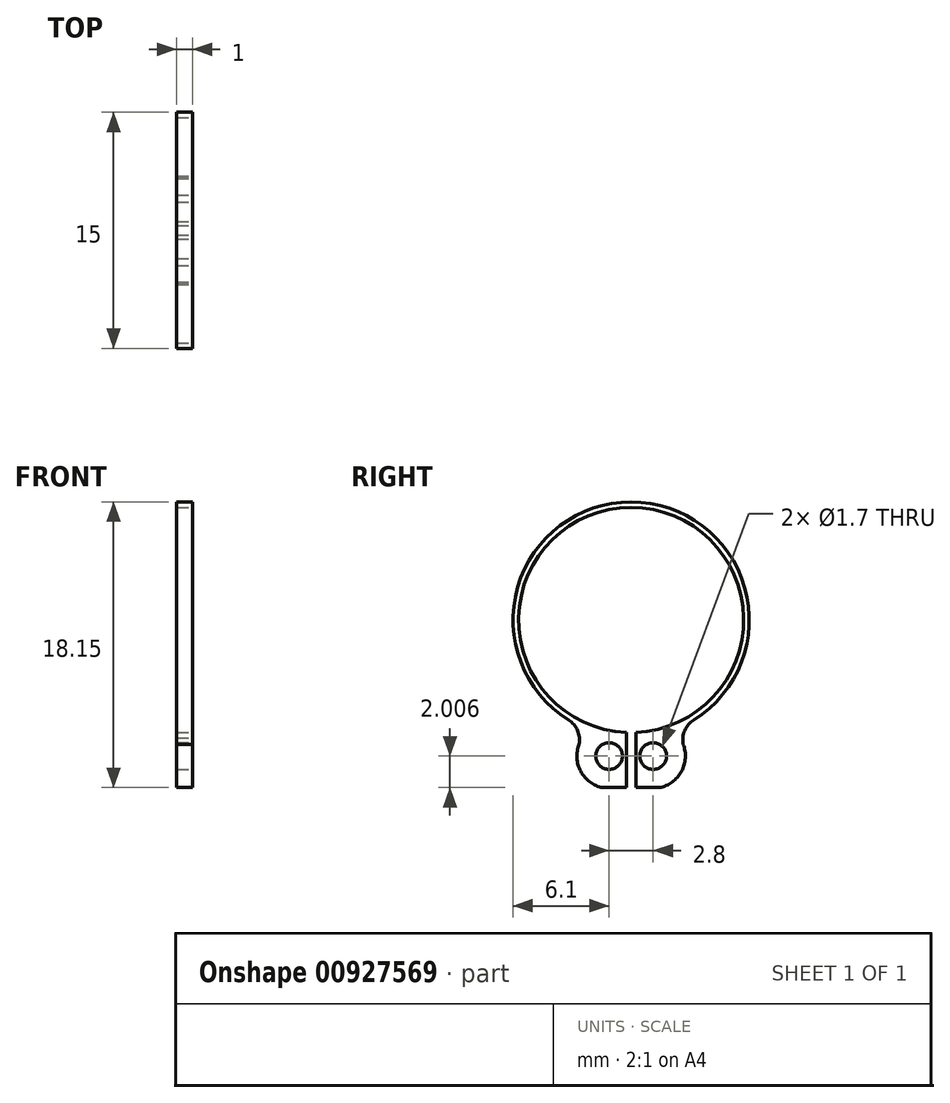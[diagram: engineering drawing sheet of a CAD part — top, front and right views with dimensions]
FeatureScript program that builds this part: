
annotation { "Feature Type Name" : "Feature", "Feature Type Description" : "" }
export const myFeature = defineFeature(function(context is Context, id is Id, definition is map)
    precondition{}
    {
        {
            var Q0;
            Q0=qCreatedBy(makeId("Right.planeOp"),FACE);
            var sketch = newSketch(context, id + "F0", { "sketchPlane" : qUnion([Q0])});
            skArc(sketch, "E0", {"start": v(0.3, -7.14) * mm, "mid": v(0, 7.15) * mm, "end": v(-0.3, -7.14) * mm});
            skArc(sketch, "E1", {"start": v(3.98, -6.36) * mm, "mid": v(0, 7.5) * mm, "end": v(-3.98, -6.36) * mm});
            skLineSegment(sketch, "E2", {"start": v(-7.47, -10.65) * mm, "end": v(-0.3, -10.65) * mm, "construction": true});
            skLineSegment(sketch, "E3", {"start": v(0.3, -7.14) * mm, "end": v(0.3, -10.65) * mm});
            skLineSegment(sketch, "E4.MirrorCS", {"start": v(-0.3, -7.14) * mm, "end": v(-0.3, -10.65) * mm});
            skCircle(sketch, "E5", {"center": v(1.4, -8.64) * mm, "radius": 0.85 * mm});
            skLineSegment(sketch, "E6", {"start": v(0.3, -10.65) * mm, "end": v(1.8, -10.65) * mm});
            skArc(sketch, "E7", {"start": v(1.8, -10.65) * mm, "mid": v(3.2, -9.62) * mm, "end": v(3.3, -7.9) * mm});
            skArc(sketch, "E8", {"start": v(3.3, -7.9) * mm, "mid": v(3.4, -7.02) * mm, "end": v(3.98, -6.36) * mm});
            skLineSegment(sketch, "E9.trimOffspring", {"start": v(0.3, -10.65) * mm, "end": v(1, -10.65) * mm, "construction": true});
            skArc(sketch, "E10.trimOffspring", {"start": v(-0.3, -7.5) * mm, "mid": v(-0.3, -7.5) * mm, "end": v(-0.3, -7.5) * mm});
            skLineSegment(sketch, "E11.trimOffspring", {"start": v(1.8, -10.65) * mm, "end": v(16.02, -10.65) * mm, "construction": true});
            skCircle(sketch, "E12.MirrorC", {"center": v(-1.4, -8.64) * mm, "radius": 0.85 * mm});
            skArc(sketch, "E13.MirrorCS", {"start": v(-3.3, -7.9) * mm, "mid": v(-3.4, -7.02) * mm, "end": v(-3.98, -6.36) * mm});
            skArc(sketch, "E14.MirrorCS", {"start": v(-1.8, -10.65) * mm, "mid": v(-3.2, -9.62) * mm, "end": v(-3.3, -7.9) * mm});
            skLineSegment(sketch, "E15.MirrorCS", {"start": v(-0.3, -10.65) * mm, "end": v(-1.8, -10.65) * mm});
            skSolve(sketch);
        }
        {
            var Q0;
            Q0 = qSketchRegion(id + "F0", true);
            extrude(context, id + "F1", {"entities" : qUnion([Q0]), "oppositeDirection" : true, "depth" : 1 * mm, "offsetDistance" : 25 * mm});
        }
    });
